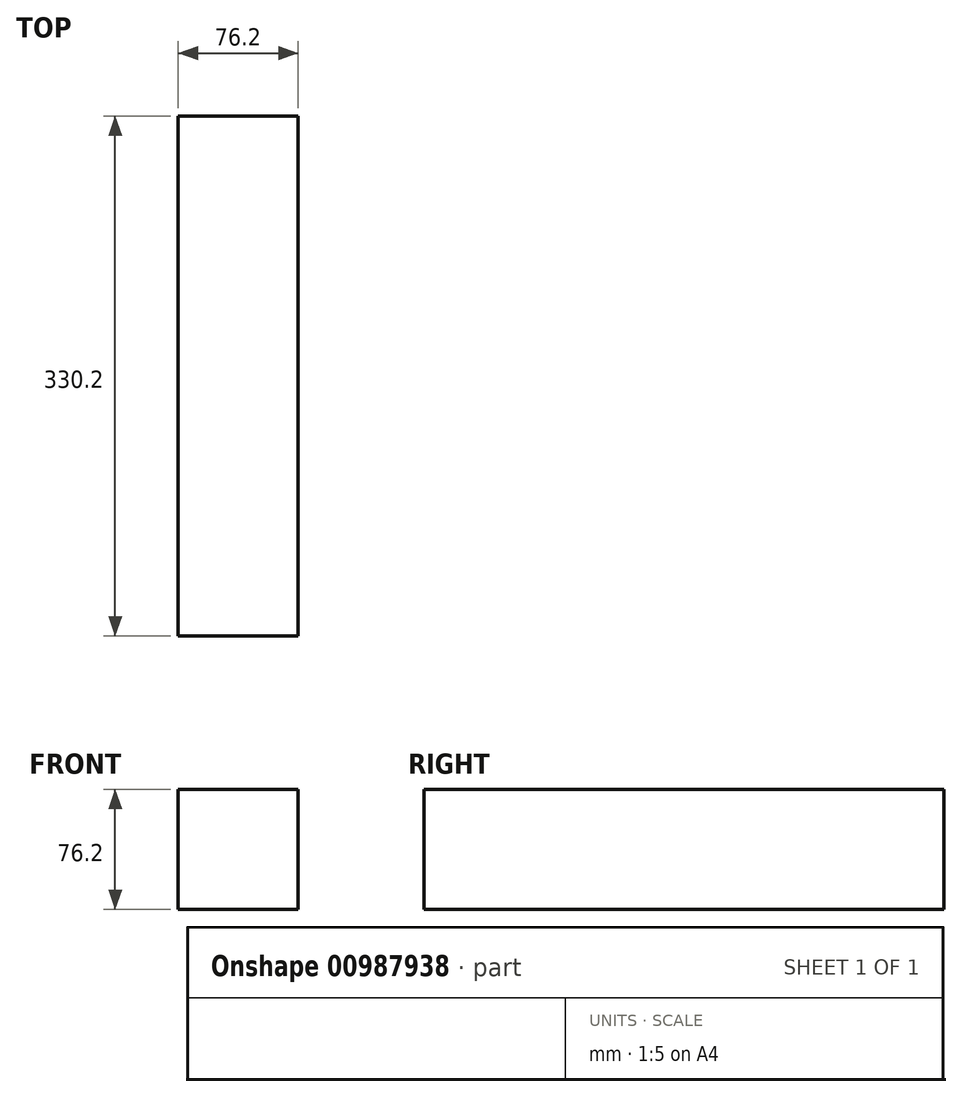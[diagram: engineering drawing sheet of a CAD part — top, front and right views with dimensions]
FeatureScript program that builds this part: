
annotation { "Feature Type Name" : "Feature", "Feature Type Description" : "" }
export const myFeature = defineFeature(function(context is Context, id is Id, definition is map)
    precondition{}
    {
        {
            var Q0;
            Q0=qCreatedBy(makeId("Front.planeOp"),FACE);
            var sketch = newSketch(context, id + "F0", { "sketchPlane" : qUnion([Q0])});
            skLineSegment(sketch, "E0.bottom", {"start": v(0, 0) * mm, "end": v(76.2, 0) * mm});
            skLineSegment(sketch, "E0.top", {"start": v(0, 76.2) * mm, "end": v(76.2, 76.2) * mm});
            skLineSegment(sketch, "E0.left", {"start": v(0, 0) * mm, "end": v(0, 76.2) * mm});
            skLineSegment(sketch, "E0.right", {"start": v(76.2, 0) * mm, "end": v(76.2, 76.2) * mm});
            skSolve(sketch);
        }
        {
            var Q0;
            Q0=makeQuery(id+"F0.imprint","IMPRINT",FACE,{"disambiguationData":[TD([[makeQuery(id+"F0.imprint","IMPRINT",EDGE,{"derivedFrom":sQuery(id+"F0.wireOp",EDGE,"E0.bottom")}),1.0]])]});
            extrude(context, id + "F1", {"entities" : qUnion([Q0]), "depth" : 127 * mm, "offsetDistance" : 25.4 * mm});
        }
        {
            var Q0;
            Q0=makeQuery(id+"F1.opExtrude","CAP_FACE",FACE,{"disambiguationData":[OSD([sQuery(id+"F0.wireOp",EDGE,"E0.bottom"),sQuery(id+"F0.wireOp",EDGE,"E0.top"),sQuery(id+"F0.wireOp",EDGE,"E0.left"),sQuery(id+"F0.wireOp",EDGE,"E0.right")])],"isStart":false});
            extrude(context, id + "F2", {"entities" : qUnion([Q0]), "operationType" : NewBodyOperationType.ADD, "depth" : 76.2 * mm, "offsetDistance" : 25.4 * mm});
        }
        {
            var Q0;
            Q0=makeQuery(id+"F1.opExtrude","CAP_FACE",FACE,{"disambiguationData":[OSD([sQuery(id+"F0.wireOp",EDGE,"E0.bottom"),sQuery(id+"F0.wireOp",EDGE,"E0.top"),sQuery(id+"F0.wireOp",EDGE,"E0.left"),sQuery(id+"F0.wireOp",EDGE,"E0.right")])],"isStart":true});
            extrude(context, id + "F3", {"entities" : qUnion([Q0]), "operationType" : NewBodyOperationType.ADD, "depth" : 127 * mm, "offsetDistance" : 25.4 * mm});
        }
    });
